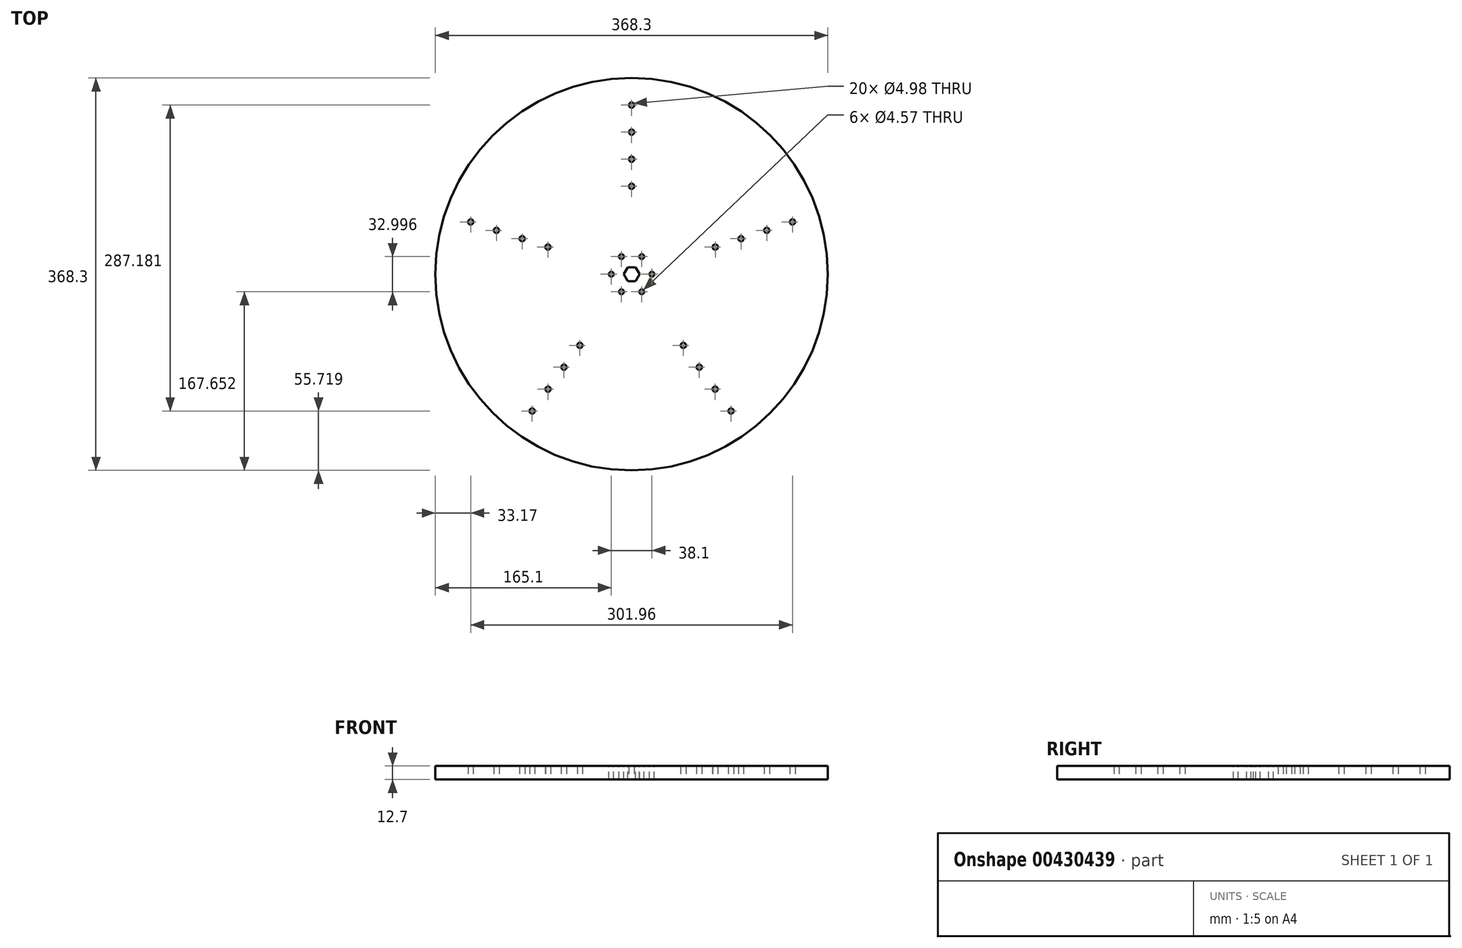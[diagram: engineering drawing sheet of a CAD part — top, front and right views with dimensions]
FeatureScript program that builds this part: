
annotation { "Feature Type Name" : "Feature", "Feature Type Description" : "" }
export const myFeature = defineFeature(function(context is Context, id is Id, definition is map)
    precondition{}
    {
        {
            var Q0;
            Q0=qCreatedBy(makeId("Top.planeOp"),FACE);
            var sketch = newSketch(context, id + "F0", { "sketchPlane" : qUnion([Q0])});
            skLineSegment(sketch, "E0", {"start": v(-174.54, 58.71) * mm, "end": v(-174.54, 58.71) * mm});
            skArc(sketch, "E1.cCircle", {"start": v(-174.54, 58.71) * mm, "mid": v(-175.72, -55.1) * mm, "end": v(-109.78, -147.85) * mm});
            skLineSegment(sketch, "E1.0", {"start": v(133.8, -184.15) * mm, "end": v(-133.8, -184.15) * mm, "construction": true});
            skLineSegment(sketch, "E1.1", {"start": v(-133.8, -184.15) * mm, "end": v(-216.48, 70.34) * mm, "construction": true});
            skLineSegment(sketch, "E1.2", {"start": v(-216.48, 70.34) * mm, "end": v(0, 227.62) * mm, "construction": true});
            skLineSegment(sketch, "E1.3", {"start": v(0, 227.62) * mm, "end": v(216.48, 70.34) * mm, "construction": true});
            skLineSegment(sketch, "E1.4", {"start": v(216.48, 70.34) * mm, "end": v(133.8, -184.15) * mm, "construction": true});
            skPoint(sketch, "E1.0.midPoint", {"position": v(0, -184.15) * mm});
            skLineSegment(sketch, "E2", {"start": v(0, 227.62) * mm, "end": v(0, 0) * mm, "construction": true});
            skLineSegment(sketch, "E3", {"start": v(-216.48, 70.34) * mm, "end": v(0, 0) * mm, "construction": true});
            skLineSegment(sketch, "E4", {"start": v(-133.8, -184.15) * mm, "end": v(0, 0) * mm, "construction": true});
            skLineSegment(sketch, "E5", {"start": v(133.8, -184.15) * mm, "end": v(0, 0) * mm, "construction": true});
            skLineSegment(sketch, "E6", {"start": v(216.48, 70.34) * mm, "end": v(0, 0) * mm, "construction": true});
            skLineSegment(sketch, "E7.bottom", {"start": v(1.9, 57.15) * mm, "end": v(-1.9, 57.15) * mm, "construction": true});
            skLineSegment(sketch, "E7.top", {"start": v(1.9, 209.55) * mm, "end": v(-1.9, 209.55) * mm, "construction": true});
            skLineSegment(sketch, "E7.left", {"start": v(1.9, 57.15) * mm, "end": v(1.9, 209.55) * mm, "construction": true});
            skLineSegment(sketch, "E7.right", {"start": v(-1.9, 57.15) * mm, "end": v(-1.9, 209.55) * mm, "construction": true});
            skArc(sketch, "E8.trimOffspring", {"start": v(-109.78, -147.85) * mm, "mid": v(175.72, 55.1) * mm, "end": v(-174.54, 58.71) * mm});
            skCircle(sketch, "E9", {"center": v(0, 82.55) * mm, "radius": 2.49 * mm});
            skCircle(sketch, "E10.0.1.0", {"center": v(0, 107.95) * mm, "radius": 2.49 * mm});
            skCircle(sketch, "E10.0.2.0", {"center": v(0, 133.35) * mm, "radius": 2.49 * mm});
            skLineSegment(sketch, "E10.direction1", {"start": v(0, 82.55) * mm, "end": v(25.4, 82.55) * mm, "construction": true});
            skLineSegment(sketch, "E10.direction2", {"start": v(0, 82.55) * mm, "end": v(0, 107.95) * mm, "construction": true});
            skCircle(sketch, "E11.0.0.3", {"center": v(0, 158.75) * mm, "radius": 2.49 * mm});
            skCircle(sketch, "E12.1.0", {"center": v(-78.5, 25.5) * mm, "radius": 2.49 * mm});
            skCircle(sketch, "E12.1.1", {"center": v(-102.67, 33.36) * mm, "radius": 2.49 * mm});
            skCircle(sketch, "E12.1.2", {"center": v(-126.82, 41.2) * mm, "radius": 2.49 * mm});
            skCircle(sketch, "E12.1.3", {"center": v(-150.98, 49.06) * mm, "radius": 2.49 * mm});
            skCircle(sketch, "E12.2.0", {"center": v(-48.52, -66.78) * mm, "radius": 2.49 * mm});
            skCircle(sketch, "E12.2.1", {"center": v(-63.45, -87.33) * mm, "radius": 2.49 * mm});
            skCircle(sketch, "E12.2.2", {"center": v(-78.38, -107.88) * mm, "radius": 2.49 * mm});
            skCircle(sketch, "E12.2.3", {"center": v(-93.31, -128.43) * mm, "radius": 2.49 * mm});
            skCircle(sketch, "E12.3.0", {"center": v(48.52, -66.78) * mm, "radius": 2.49 * mm});
            skCircle(sketch, "E12.3.1", {"center": v(63.45, -87.33) * mm, "radius": 2.49 * mm});
            skCircle(sketch, "E12.3.2", {"center": v(78.38, -107.88) * mm, "radius": 2.49 * mm});
            skCircle(sketch, "E12.3.3", {"center": v(93.31, -128.43) * mm, "radius": 2.49 * mm});
            skCircle(sketch, "E12.4.0", {"center": v(78.5, 25.5) * mm, "radius": 2.49 * mm});
            skCircle(sketch, "E12.4.1", {"center": v(102.67, 33.36) * mm, "radius": 2.49 * mm});
            skCircle(sketch, "E12.4.2", {"center": v(126.82, 41.2) * mm, "radius": 2.49 * mm});
            skCircle(sketch, "E12.4.3", {"center": v(150.98, 49.06) * mm, "radius": 2.49 * mm});
            skLineSegment(sketch, "E13", {"start": v(-1.9, 177.8) * mm, "end": v(1.9, 177.8) * mm, "construction": true});
            skSolve(sketch);
        }
        {
            var Q0;
            Q0=makeQuery(id+"F0.imprint","IMPRINT",FACE,{"disambiguationData":[TD([[makeQuery(id+"F0.imprint","IMPRINT",EDGE,{"derivedFrom":sQuery(id+"F0.wireOp",EDGE,"E1.cCircle")}),1.0]])]});
            extrude(context, id + "F1", {"entities" : qUnion([Q0]), "depth" : 12.7 * mm, "offsetDistance" : 25.4 * mm});
        }
        {
            var Q0;
            Q0=makeQuery(id+"F1.opExtrude","CAP_FACE",FACE,{"disambiguationData":[OSD([sQuery(id+"F0.wireOp",EDGE,"E1.cCircle"),sQuery(id+"F0.wireOp",EDGE,"E8.trimOffspring"),sQuery(id+"F0.wireOp",EDGE,"E9"),sQuery(id+"F0.wireOp",EDGE,"E10.0.1.0"),sQuery(id+"F0.wireOp",EDGE,"E10.0.2.0"),sQuery(id+"F0.wireOp",EDGE,"E11.0.0.3"),sQuery(id+"F0.wireOp",EDGE,"E12.1.0"),sQuery(id+"F0.wireOp",EDGE,"E12.1.1"),sQuery(id+"F0.wireOp",EDGE,"E12.1.2"),sQuery(id+"F0.wireOp",EDGE,"E12.1.3"),sQuery(id+"F0.wireOp",EDGE,"E12.2.0"),sQuery(id+"F0.wireOp",EDGE,"E12.2.1"),sQuery(id+"F0.wireOp",EDGE,"E12.2.2"),sQuery(id+"F0.wireOp",EDGE,"E12.2.3"),sQuery(id+"F0.wireOp",EDGE,"E12.3.0"),sQuery(id+"F0.wireOp",EDGE,"E12.3.1"),sQuery(id+"F0.wireOp",EDGE,"E12.3.2"),sQuery(id+"F0.wireOp",EDGE,"E12.3.3"),sQuery(id+"F0.wireOp",EDGE,"E12.4.0"),sQuery(id+"F0.wireOp",EDGE,"E12.4.1"),sQuery(id+"F0.wireOp",EDGE,"E12.4.2"),sQuery(id+"F0.wireOp",EDGE,"E12.4.3")])],"isStart":false});
            var sketch = newSketch(context, id + "F2", { "sketchPlane" : qUnion([Q0])});
            skCircle(sketch, "E14.cCircle", {"center": v(0, 0) * mm, "radius": 6.41 * mm, "construction": true});
            skLineSegment(sketch, "E14.0", {"start": v(-3.7, 6.41) * mm, "end": v(3.7, 6.41) * mm});
            skLineSegment(sketch, "E14.1", {"start": v(3.7, 6.41) * mm, "end": v(7.4, 0) * mm});
            skLineSegment(sketch, "E14.2", {"start": v(7.4, 0) * mm, "end": v(3.7, -6.41) * mm});
            skLineSegment(sketch, "E14.3", {"start": v(3.7, -6.41) * mm, "end": v(-3.7, -6.41) * mm});
            skLineSegment(sketch, "E14.4", {"start": v(-3.7, -6.41) * mm, "end": v(-7.4, 0) * mm});
            skLineSegment(sketch, "E14.5", {"start": v(-7.4, 0) * mm, "end": v(-3.7, 6.41) * mm});
            skPoint(sketch, "E14.0.midPoint", {"position": v(0, 6.41) * mm});
            skCircle(sketch, "E15", {"center": v(-19.05, 0) * mm, "radius": 2.29 * mm});
            skCircle(sketch, "E16.1.0", {"center": v(-9.53, -16.5) * mm, "radius": 2.29 * mm});
            skCircle(sketch, "E16.2.0", {"center": v(9.52, -16.5) * mm, "radius": 2.29 * mm});
            skCircle(sketch, "E16.3.0", {"center": v(19.05, 0) * mm, "radius": 2.29 * mm});
            skCircle(sketch, "E16.4.0", {"center": v(9.53, 16.5) * mm, "radius": 2.29 * mm});
            skCircle(sketch, "E16.5.0", {"center": v(-9.52, 16.5) * mm, "radius": 2.29 * mm});
            skSolve(sketch);
        }
        {
            var Q0;
            Q0 = qSketchRegion(id + "F2", true);
            var Q1;
            Q1=makeQuery(id+"F1.opExtrude","CAP_FACE",FACE,{"disambiguationData":[OSD([sQuery(id+"F0.wireOp",EDGE,"E1.cCircle"),sQuery(id+"F0.wireOp",EDGE,"E8.trimOffspring"),sQuery(id+"F0.wireOp",EDGE,"E9"),sQuery(id+"F0.wireOp",EDGE,"E10.0.1.0"),sQuery(id+"F0.wireOp",EDGE,"E10.0.2.0"),sQuery(id+"F0.wireOp",EDGE,"E11.0.0.3"),sQuery(id+"F0.wireOp",EDGE,"E12.1.0"),sQuery(id+"F0.wireOp",EDGE,"E12.1.1"),sQuery(id+"F0.wireOp",EDGE,"E12.1.2"),sQuery(id+"F0.wireOp",EDGE,"E12.1.3"),sQuery(id+"F0.wireOp",EDGE,"E12.2.0"),sQuery(id+"F0.wireOp",EDGE,"E12.2.1"),sQuery(id+"F0.wireOp",EDGE,"E12.2.2"),sQuery(id+"F0.wireOp",EDGE,"E12.2.3"),sQuery(id+"F0.wireOp",EDGE,"E12.3.0"),sQuery(id+"F0.wireOp",EDGE,"E12.3.1"),sQuery(id+"F0.wireOp",EDGE,"E12.3.2"),sQuery(id+"F0.wireOp",EDGE,"E12.3.3"),sQuery(id+"F0.wireOp",EDGE,"E12.4.0"),sQuery(id+"F0.wireOp",EDGE,"E12.4.1"),sQuery(id+"F0.wireOp",EDGE,"E12.4.2"),sQuery(id+"F0.wireOp",EDGE,"E12.4.3")])],"isStart":true});
            extrude(context, id + "F3", {"entities" : qUnion([Q0]), "operationType" : NewBodyOperationType.REMOVE, "endBound" : BoundingType.UP_TO_SURFACE, "oppositeDirection" : true, "endBoundEntityFace" : qUnion([Q1]), "depth" : 25.4 * mm, "offsetDistance" : 25.4 * mm});
        }
    });
